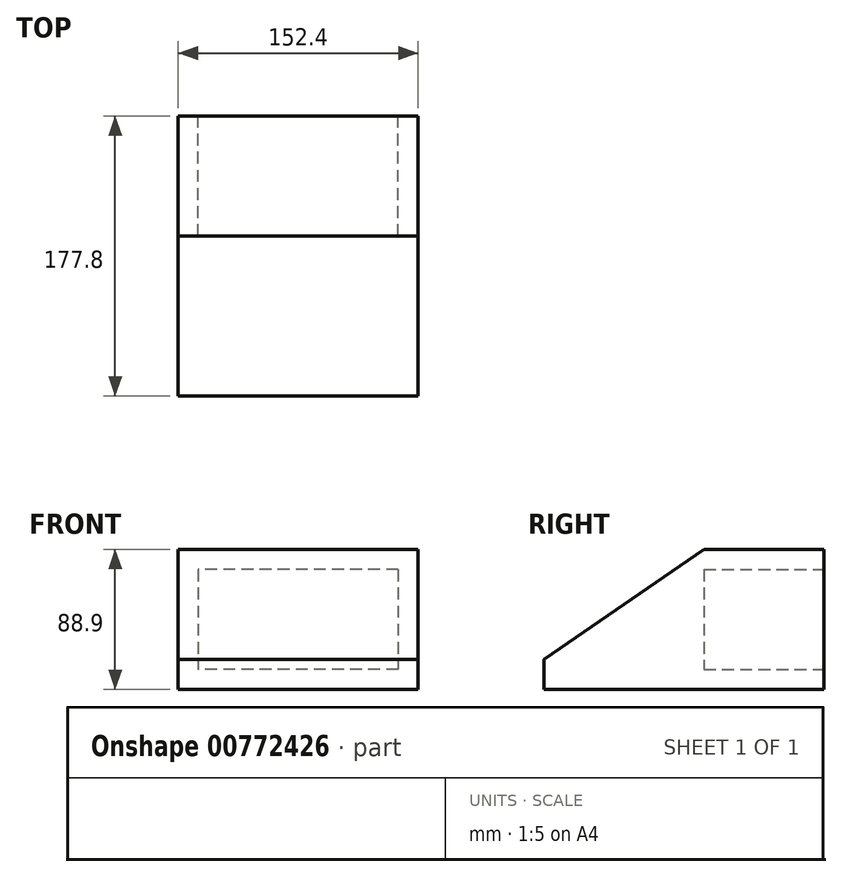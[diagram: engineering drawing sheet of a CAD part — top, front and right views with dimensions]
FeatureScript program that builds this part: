
annotation { "Feature Type Name" : "Feature", "Feature Type Description" : "" }
export const myFeature = defineFeature(function(context is Context, id is Id, definition is map)
    precondition{}
    {
        {
            var Q0;
            Q0=qCreatedBy(makeId("Top.planeOp"),FACE);
            var sketch = newSketch(context, id + "F0", { "sketchPlane" : qUnion([Q0])});
            skLineSegment(sketch, "E0.bottom", {"start": v(-74.85, 107.47) * mm, "end": v(77.55, 107.47) * mm});
            skLineSegment(sketch, "E0.top", {"start": v(-74.85, -70.33) * mm, "end": v(77.55, -70.33) * mm});
            skLineSegment(sketch, "E0.left", {"start": v(-74.85, 107.47) * mm, "end": v(-74.85, -70.33) * mm});
            skLineSegment(sketch, "E0.right", {"start": v(77.55, 107.47) * mm, "end": v(77.55, -70.33) * mm});
            skSolve(sketch);
        }
        {
            var Q0;
            Q0=makeQuery(id+"F0.imprint","IMPRINT",FACE,{"disambiguationData":[TD([[makeQuery(id+"F0.imprint","IMPRINT",EDGE,{"derivedFrom":sQuery(id+"F0.wireOp",EDGE,"E0.bottom")}),-1.0]])]});
            extrude(context, id + "F1", {"entities" : qUnion([Q0]), "depth" : 88.9 * mm, "offsetDistance" : 25.4 * mm});
        }
        {
            var Q0;
            Q0=makeQuery(id+"F1.opExtrude","CAP_EDGE",EDGE,{"disambiguationData":[OSD([sQuery(id+"F0.wireOp",EDGE,"E0.top")])],"isStart":false});
            chamfer(context, id + "F2", {"entities" : qUnion([Q0]), "chamferType" : ChamferType.TWO_OFFSETS, "width1" : 101.6 * mm, "oppositeDirection" : false, "width2" : 69.85 * mm, "tangentPropagation" : true});
        }
        {
            var Q0;
            Q0=makeQuery(id+"F1.opExtrude","SWEPT_FACE",FACE,{"disambiguationData":[OSD([sQuery(id+"F0.wireOp",EDGE,"E0.bottom")])]});
            var sketch = newSketch(context, id + "F3", { "sketchPlane" : qUnion([Q0])});
            skLineSegment(sketch, "E1.bottom", {"start": v(-64.85, 76.2) * mm, "end": v(62.15, 76.2) * mm});
            skLineSegment(sketch, "E1.top", {"start": v(-64.85, 12.7) * mm, "end": v(62.15, 12.7) * mm});
            skLineSegment(sketch, "E1.left", {"start": v(-64.85, 76.2) * mm, "end": v(-64.85, 12.7) * mm});
            skLineSegment(sketch, "E1.right", {"start": v(62.15, 76.2) * mm, "end": v(62.15, 12.7) * mm});
            skSolve(sketch);
        }
        {
            var Q0;
            Q0=makeQuery(id+"F3.imprint","IMPRINT",FACE,{"disambiguationData":[TD([[makeQuery(id+"F3.imprint","IMPRINT",EDGE,{"derivedFrom":sQuery(id+"F3.wireOp",EDGE,"E1.bottom")}),-1.0]])]});
            extrude(context, id + "F4", {"entities" : qUnion([Q0]), "operationType" : NewBodyOperationType.REMOVE, "oppositeDirection" : true, "depth" : 76.2 * mm, "offsetDistance" : 25.4 * mm});
        }
    });
